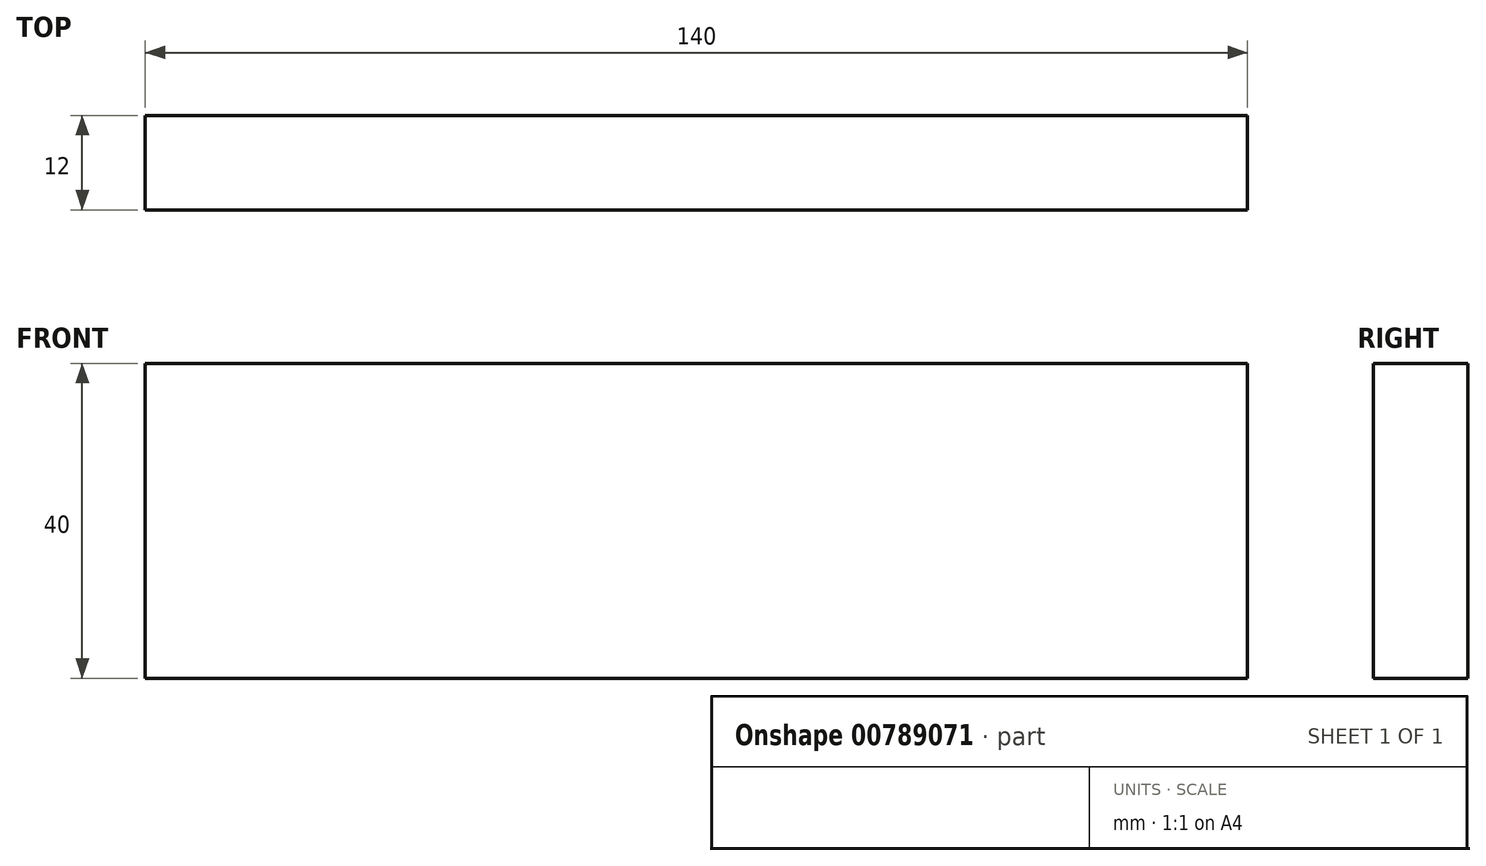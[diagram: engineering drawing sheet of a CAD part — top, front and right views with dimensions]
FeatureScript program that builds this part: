
annotation { "Feature Type Name" : "Feature", "Feature Type Description" : "" }
export const myFeature = defineFeature(function(context is Context, id is Id, definition is map)
    precondition{}
    {
        {
            var Q0;
            Q0=qCreatedBy(makeId("Right.planeOp"),FACE);
            var sketch = newSketch(context, id + "F0", { "sketchPlane" : qUnion([Q0])});
            skLineSegment(sketch, "E0.bottom", {"start": v(0, 0) * mm, "end": v(-12, 0) * mm});
            skLineSegment(sketch, "E0.top", {"start": v(0, 40) * mm, "end": v(-12, 40) * mm});
            skLineSegment(sketch, "E0.left", {"start": v(0, 0) * mm, "end": v(0, 40) * mm});
            skLineSegment(sketch, "E0.right", {"start": v(-12, 0) * mm, "end": v(-12, 40) * mm});
            skSolve(sketch);
        }
        {
            var Q0;
            Q0=makeQuery(id+"F0.imprint","IMPRINT",FACE,{"disambiguationData":[TD([[makeQuery(id+"F0.imprint","IMPRINT",EDGE,{"derivedFrom":sQuery(id+"F0.wireOp",EDGE,"E0.bottom")}),-1.0]])]});
            extrude(context, id + "F1", {"entities" : qUnion([Q0]), "depth" : 140 * mm, "offsetDistance" : 25 * mm});
        }
    });
